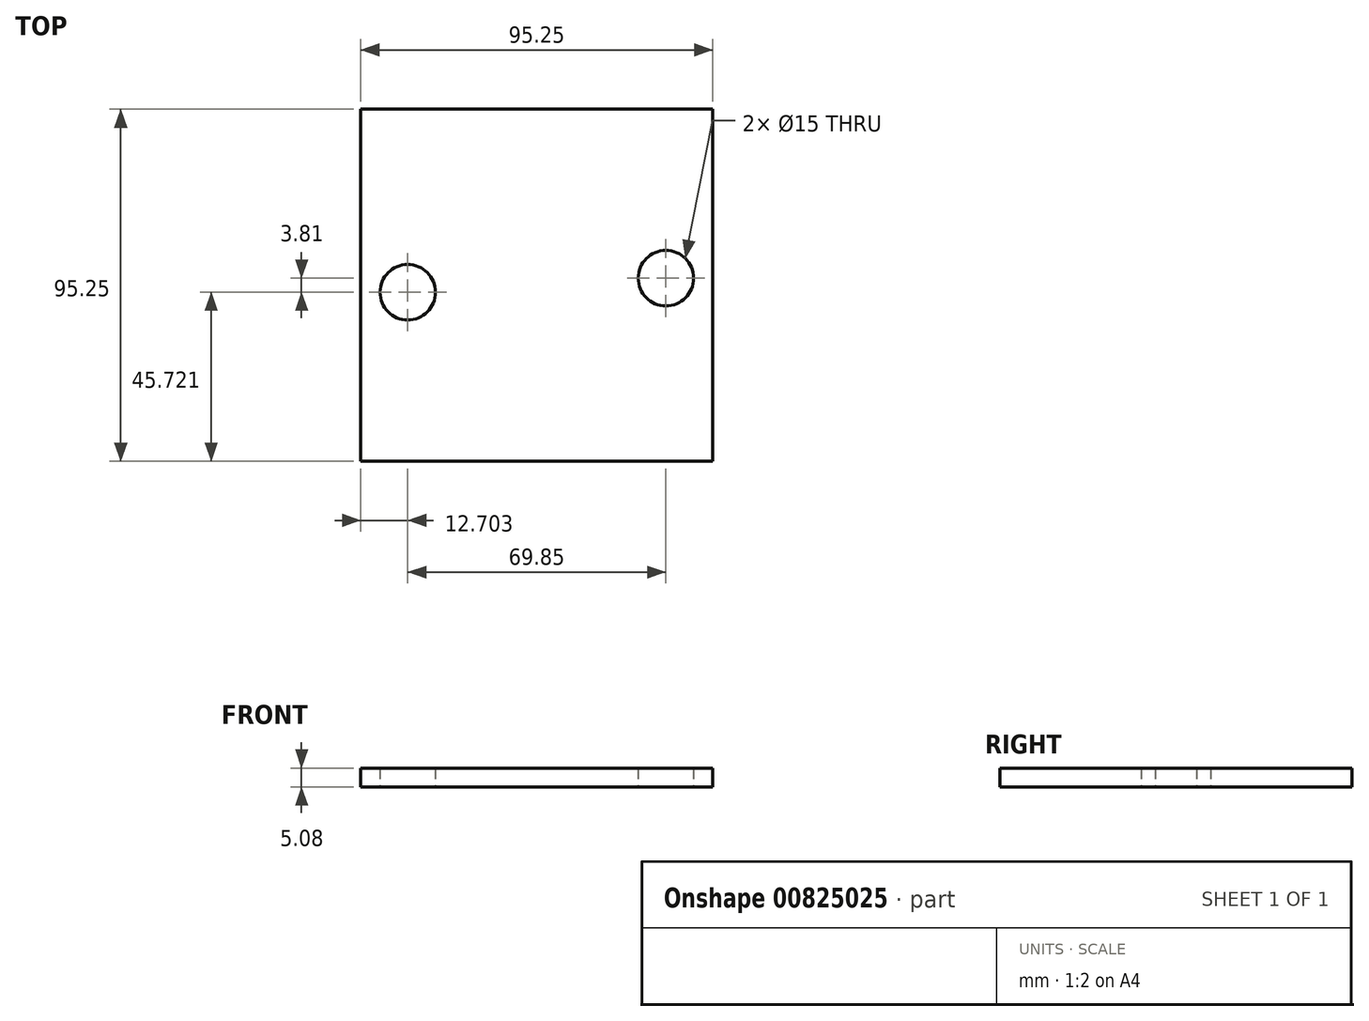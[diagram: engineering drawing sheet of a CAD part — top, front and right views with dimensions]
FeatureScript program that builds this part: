
annotation { "Feature Type Name" : "Feature", "Feature Type Description" : "" }
export const myFeature = defineFeature(function(context is Context, id is Id, definition is map)
    precondition{}
    {
        {
            var Q0;
            Q0=qCreatedBy(makeId("Top.planeOp"),FACE);
            var sketch = newSketch(context, id + "F0", { "sketchPlane" : qUnion([Q0])});
            skLineSegment(sketch, "E0.0", {"start": v(11.04, 5.36) * mm, "end": v(11.04, -42.27) * mm});
            skLineSegment(sketch, "E1.0", {"start": v(-84.2, 52.98) * mm, "end": v(11.04, 52.98) * mm});
            skLineSegment(sketch, "E2.0", {"start": v(-84.2, -42.27) * mm, "end": v(-84.2, 52.98) * mm});
            skLineSegment(sketch, "E3.0", {"start": v(11.04, -42.27) * mm, "end": v(-84.2, -42.27) * mm});
            skCircle(sketch, "E4", {"center": v(-1.66, 7.26) * mm, "radius": 7.5 * mm});
            skLineSegment(sketch, "E5", {"start": v(11.04, 52.98) * mm, "end": v(11.04, 29.17) * mm});
            skLineSegment(sketch, "E6", {"start": v(11.04, 29.17) * mm, "end": v(11.04, 5.36) * mm});
            skCircle(sketch, "E7.MirrorC", {"center": v(-71.5, 3.45) * mm, "radius": 7.5 * mm});
            skSolve(sketch);
        }
        {
            var Q0;
            Q0=makeQuery(id+"F0.imprint","IMPRINT",FACE,{"disambiguationData":[TD([[makeQuery(id+"F0.imprint","IMPRINT",EDGE,{"derivedFrom":sQuery(id+"F0.wireOp",EDGE,"E0.0")}),-1.0]])]});
            extrude(context, id + "F1", {"entities" : qUnion([Q0]), "depth" : 5.08 * mm, "offsetDistance" : 25.4 * mm});
        }
    });
